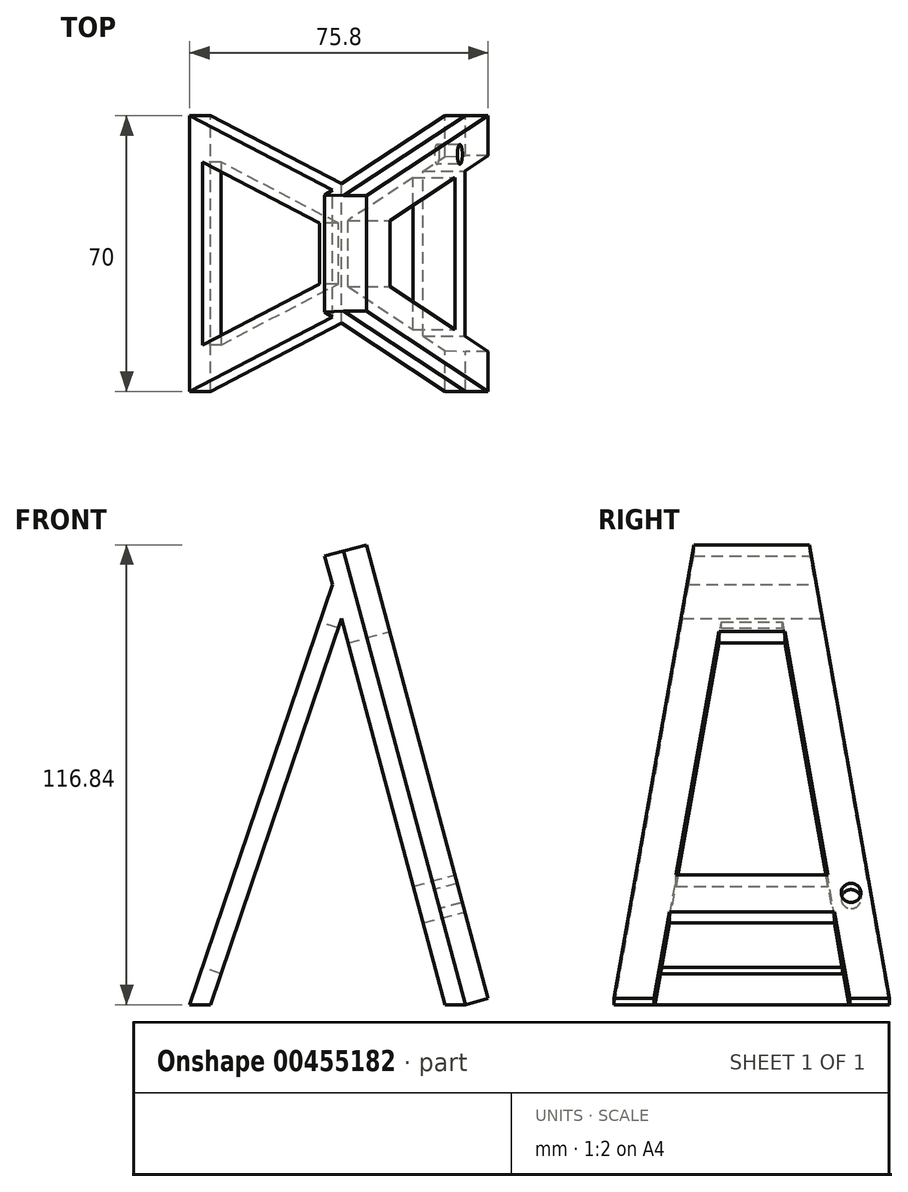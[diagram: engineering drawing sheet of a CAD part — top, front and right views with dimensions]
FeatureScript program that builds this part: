
annotation { "Feature Type Name" : "Feature", "Feature Type Description" : "" }
export const myFeature = defineFeature(function(context is Context, id is Id, definition is map)
    precondition{}
    {
        {
            var Q0;
            Q0=qCreatedBy(makeId("Front.planeOp"),FACE);
            var sketch = newSketch(context, id + "F0", { "sketchPlane" : qUnion([Q0])});
            skLineSegment(sketch, "E0", {"start": v(70, 0) * mm, "end": v(39.1, 115.28) * mm});
            skLineSegment(sketch, "E1", {"start": v(39.1, 115.28) * mm, "end": v(63.12, 25.69) * mm});
            skPoint(sketch, "E2", {"position": v(39.1, 115.28) * mm});
            skLineSegment(sketch, "E3", {"start": v(36.22, 106.76) * mm, "end": v(0, 0) * mm});
            skLineSegment(sketch, "E4", {"start": v(34.28, 114) * mm, "end": v(36.22, 106.76) * mm});
            skLineSegment(sketch, "E5", {"start": v(0, 0) * mm, "end": v(5.28, 0) * mm});
            skLineSegment(sketch, "E6", {"start": v(5.28, 0) * mm, "end": v(38.55, 98.06) * mm});
            skLineSegment(sketch, "E7.trimOffspring", {"start": v(64.82, 0) * mm, "end": v(70, 0) * mm});
            skPoint(sketch, "E8.orphan", {"position": v(44.39, 115.28) * mm});
            skLineSegment(sketch, "E9.trimOffspring", {"start": v(38.55, 98.06) * mm, "end": v(64.82, 0) * mm});
            skPoint(sketch, "E10.end.orphan", {"position": v(10.27, 203.59) * mm});
            skPoint(sketch, "E10.start.orphan", {"position": v(15.1, 204.88) * mm});
            skLineSegment(sketch, "E11", {"start": v(39.1, 115.28) * mm, "end": v(34.28, 114) * mm});
            skPoint(sketch, "E12.start.orphan", {"position": v(23.25, 155.17) * mm});
            skSolve(sketch);
        }
        {
            var Q0;
            Q0=makeQuery(id+"F0.imprint","IMPRINT",FACE,{"disambiguationData":[TD([[makeQuery(id+"F0.imprint","IMPRINT",EDGE,{"derivedFrom":sQuery(id+"F0.wireOp",EDGE,"E0")}),1.0]])]});
            extrude(context, id + "F1", {"entities" : qUnion([Q0]), "depth" : 70 * mm});
        }
        {
            var Q0;
            Q0=qCreatedBy(makeId("Right.planeOp"),FACE);
            var sketch = newSketch(context, id + "F2", { "sketchPlane" : qUnion([Q0])});
            skLineSegment(sketch, "E13", {"start": v(0, 0) * mm, "end": v(-31.1, 176.4) * mm});
            skLineSegment(sketch, "E14.MirrorCS", {"start": v(-70, 0) * mm, "end": v(-38.9, 176.4) * mm});
            skPoint(sketch, "E15.0.2.start.orphan", {"position": v(-70, 115.28) * mm});
            skPoint(sketch, "E16.orphan", {"position": v(-35, 115.28) * mm});
            skPoint(sketch, "E15.0.0.end.orphan", {"position": v(0, 115.28) * mm});
            skPoint(sketch, "E17.orphan", {"position": v(0, 0) * mm});
            skPoint(sketch, "E15.0.3.start.orphan", {"position": v(-70, 0) * mm});
            skLineSegment(sketch, "E18", {"start": v(-38.9, 176.4) * mm, "end": v(-111.55, 176.4) * mm});
            skLineSegment(sketch, "E19", {"start": v(-111.55, 176.4) * mm, "end": v(-111.55, -12.97) * mm});
            skLineSegment(sketch, "E20", {"start": v(-111.55, -12.97) * mm, "end": v(-70, 0) * mm});
            skLineSegment(sketch, "E21", {"start": v(0, 0) * mm, "end": v(48.43, -5.19) * mm});
            skLineSegment(sketch, "E22", {"start": v(48.43, -5.19) * mm, "end": v(65.81, 203.33) * mm});
            skLineSegment(sketch, "E23", {"start": v(65.81, 203.33) * mm, "end": v(-31.1, 176.4) * mm});
            skSolve(sketch);
        }
        {
            var Q0;
            Q0 = qSketchRegion(id + "F2", true);
            extrude(context, id + "F3", {"entities" : qUnion([Q0]), "operationType" : NewBodyOperationType.REMOVE, "endBound" : BoundingType.THROUGH_ALL, "depth" : 25 * mm});
        }
        {
            var Q0;
            Q0=makeQuery(id+"F1.opExtrude","SWEPT_FACE",FACE,{"disambiguationData":[OSD([sQuery(id+"F0.wireOp",EDGE,"E3")])]});
            var sketch = newSketch(context, id + "F4", { "sketchPlane" : qUnion([Q0])});
            skLineSegment(sketch, "E24.0", {"start": v(42.7, 102.74) * mm, "end": v(27.3, 102.74) * mm});
            skLineSegment(sketch, "E24.1", {"start": v(58.2, 10) * mm, "end": v(42.7, 102.74) * mm});
            skLineSegment(sketch, "E24.2", {"start": v(11.8, 10) * mm, "end": v(58.2, 10) * mm});
            skLineSegment(sketch, "E24.3", {"start": v(27.3, 102.74) * mm, "end": v(11.8, 10) * mm});
            skSolve(sketch);
        }
        {
            var Q0;
            Q0=makeQuery(id+"F4.imprint","IMPRINT",FACE,{"disambiguationData":[TD([[makeQuery(id+"F4.imprint","IMPRINT",EDGE,{"derivedFrom":sQuery(id+"F4.wireOp",EDGE,"E24.0")}),1.0]])]});
            extrude(context, id + "F5", {"entities" : qUnion([Q0]), "operationType" : NewBodyOperationType.REMOVE, "oppositeDirection" : true, "depth" : 5 * mm});
        }
        {
            var Q0;
            Q0=makeQuery(id+"F1.opExtrude","SWEPT_FACE",FACE,{"disambiguationData":[OSD([sQuery(id+"F0.wireOp",EDGE,"E0"),sQuery(id+"F0.wireOp",EDGE,"E1")])]});
            var sketch = newSketch(context, id + "F6", { "sketchPlane" : qUnion([Q0])});
            skLineSegment(sketch, "E25.1", {"start": v(-43.42, 78.41) * mm, "end": v(-54.32, 14.37) * mm});
            skLineSegment(sketch, "E25.2", {"start": v(-11.85, -8.12) * mm, "end": v(-14.02, 4.67) * mm});
            skLineSegment(sketch, "E26", {"start": v(-43.42, 78.41) * mm, "end": v(-26.58, 78.41) * mm});
            skCircle(sketch, "E27", {"center": v(-60.2, 9.67) * mm, "radius": 2.5 * mm});
            skPoint(sketch, "E28.orphan", {"position": v(-55.12, 9.67) * mm});
            skPoint(sketch, "E29.end.orphan", {"position": v(-65.27, 9.67) * mm});
            skLineSegment(sketch, "E30", {"start": v(-55.98, 4.67) * mm, "end": v(-14.02, 4.67) * mm});
            skLineSegment(sketch, "E31.0", {"start": v(-54.32, 14.37) * mm, "end": v(-15.68, 14.37) * mm});
            skLineSegment(sketch, "E32.trimOffspring", {"start": v(-15.68, 14.37) * mm, "end": v(-26.58, 78.41) * mm});
            skLineSegment(sketch, "E33.trimOffspring", {"start": v(-55.98, 4.67) * mm, "end": v(-58.15, -8.12) * mm});
            skLineSegment(sketch, "E34", {"start": v(-58.15, -8.12) * mm, "end": v(-60.75, -23.35) * mm});
            skPoint(sketch, "E35.end.orphan", {"position": v(-70, -18.12) * mm});
            skPoint(sketch, "E35.start.orphan", {"position": v(-64.08, -13.12) * mm});
            skLineSegment(sketch, "E36", {"start": v(-11.85, -8.12) * mm, "end": v(-9, -24.85) * mm});
            skPoint(sketch, "E37.orphan", {"position": v(-35, -8.12) * mm});
            skPoint(sketch, "E38.start.orphan", {"position": v(-35, 78.41) * mm});
            skLineSegment(sketch, "E39", {"start": v(-35, -8.12) * mm, "end": v(-35, 57.33) * mm, "construction": true});
            skCircle(sketch, "E40.MirrorC", {"center": v(-9.8, 9.67) * mm, "radius": 2.5 * mm});
            skSolve(sketch);
        }
        {
            var Q0;
            {var subQ6=sQuery(id+"F6.wireOp",EDGE,"E25.2");Q0=makeQuery(id+"F6.imprint","IMPRINT",FACE,{"disambiguationData":[TD([[makeQuery(id+"F6.imprint","IMPRINT",EDGE,{"derivedFrom":subQ6}),1.0]])]});}
            var Q1;
            Q1=makeQuery(id+"F6.imprint","IMPRINT",FACE,{"disambiguationData":[TD([[makeQuery(id+"F6.imprint","IMPRINT",EDGE,{"derivedFrom":sQuery(id+"F6.wireOp",EDGE,"E25.1")}),1.0]])]});
            extrude(context, id + "F7", {"entities" : qUnion([Q0, Q1]), "operationType" : NewBodyOperationType.REMOVE, "oppositeDirection" : true, "depth" : 5 * mm});
        }
        {
            var Q0;
            Q0=makeQuery(id+"F6.imprint","IMPRINT",FACE,{"disambiguationData":[TD([[makeQuery(id+"F6.imprint","IMPRINT",EDGE,{"derivedFrom":sQuery(id+"F6.wireOp",EDGE,"E27")}),1.0]])]});
            var Q1;
            Q1=makeQuery(id+"F6.imprint","IMPRINT",FACE,{"disambiguationData":[TD([[makeQuery(id+"F6.imprint","IMPRINT",EDGE,{"derivedFrom":sQuery(id+"F6.wireOp",EDGE,"E40.MirrorC")}),-1.0]])]});
            extrude(context, id + "F8", {"entities" : qUnion([Q0, Q1]), "operationType" : NewBodyOperationType.ADD, "depth" : 6 * mm});
        }
    });
